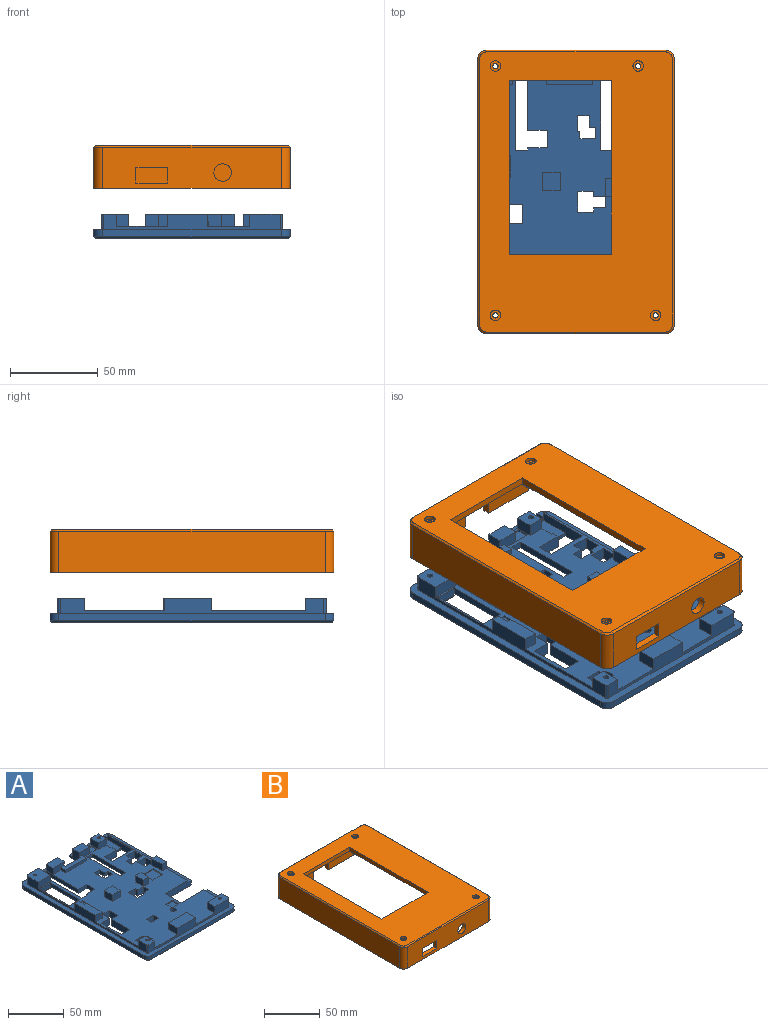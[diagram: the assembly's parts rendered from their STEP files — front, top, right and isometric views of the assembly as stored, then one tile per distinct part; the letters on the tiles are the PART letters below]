
ASSEMBLY  parts=2 mates=1
PART A: 225 faces, bbox 112x162x14 mm
  f0: plane 38.5x4mm, normal (0,1,0), area 103.3mm2, adj f14,f40,f199,f202,f211,f216,f223
  f1: plane 160x110mm, normal (0,0,-1), area 10856.5mm2, adj f25,f51,f87,f88,f89,f90,f91,f92
  f2: plane 42x4mm, normal (-1,0,0), area 168mm2, adj f3,f5,f27,f211
  f3: plane 7x4mm, normal (0,1,0), area 28mm2, adj f2,f4,f27,f211
  f4: plane 42x4mm, normal (1,0,0), area 168mm2, adj f3,f5,f27,f211
  f5: plane 7x4mm, normal (0,-1,0), area 28mm2, adj f2,f4,f27,f211
  f6: plane 6.5x4mm, normal (-1,0,0), area 26mm2, adj f7,f13,f27,f211
  f7: plane 4x3.75mm, normal (0,-1,0), area 15mm2, adj f6,f8,f27,f211
  f8: plane 6.5x4mm, normal (-1,0,0), area 26mm2, adj f7,f9,f27,f211
  f9: plane 9x4mm, normal (0,1,0), area 36mm2, adj f8,f10,f27,f211
  f10: plane 4x4mm, normal (1,0,0), area 16mm2, adj f9,f11,f27,f211
  f11: plane 4x1.25mm, normal (0,1,0), area 5mm2, adj f10,f12,f27,f211
  f12: plane 9x4mm, normal (1,0,0), area 36mm2, adj f11,f13,f27,f211
  f13: plane 6.5x4mm, normal (0,-1,0), area 26mm2, adj f6,f12,f27,f211
  f14: plane 15x11mm, normal (1,0,0), area 119.2mm2, adj f0,f16,f26,f40,f44,f70,f193,f211
  f15: plane 15x11mm, normal (-1,0,0), area 119.2mm2, adj f16,f39,f41,f43,f47,f73,f193,f211
  f16: plane 19x7mm, normal (0,1,0), area 133mm2, adj f14,f15,f193,f211
  f17: plane 40.6x4mm, normal (-1,0,0), area 162.4mm2, adj f18,f24,f27,f211
  f18: plane 11x4mm, normal (0,-1,0), area 44mm2, adj f17,f19,f27,f211
  f19: plane 10x4mm, normal (-1,0,0), area 40mm2, adj f18,f20,f27,f211
  f20: plane 11x4mm, normal (0,1,0), area 44mm2, adj f19,f21,f27,f211
  f21: plane 4x1.5mm, normal (-1,0,0), area 6mm2, adj f20,f22,f27,f211
  f22: plane 7x4mm, normal (0,1,0), area 28mm2, adj f21,f23,f27,f211
  f23: plane 52.1x4mm, normal (1,0,0), area 208.4mm2, adj f22,f24,f27,f211
  f24: plane 7x4mm, normal (0,-1,0), area 28mm2, adj f17,f23,f27,f211
  f25: plane 25.73x1mm, normal (0,0.71,-0.71), area 35.7mm2, adj f1,f47,f210,f224
  f26: plane 14.33x7mm, normal (0,-1,0), area 86.7mm2, adj f14,f27,f70,f71,f190,f193
  f27: plane 153.6x103.6mm, normal (0,0,1), area 10230.7mm2, adj f2,f3,f4,f5,f6,f7,f8,f9
  f28: plane 27.15x7.8mm, normal (0,0,1), area 191.8mm2, adj f29,f30,f50,f62,f170,f173
  f29: plane 7x5.11mm, normal (0,1,0), area 35.8mm2, adj f27,f28,f50,f173
  f30: plane 19.72x7mm, normal (1,0,0), area 138mm2, adj f27,f28,f62,f170
  f31: plane 17.72x12mm, normal (1,0,0), area 160.7mm2, adj f27,f43,f67,f69,f100,f167
  f32: plane 105x6.5mm, normal (0,0,1), area 445.8mm2, adj f33,f38,f47,f56,f123,f166,f194,f200
  f33: plane 3x1mm, normal (0,-1,0), area 3mm2, adj f32,f101,f166,f167
  f34: cylinder r=1.5mm len=11.5mm, axis (0,0,1), area 108.4mm2, adj f67,f165
  f35: cylinder r=1.5mm len=11.5mm, axis (0,0,1), area 108.4mm2, adj f54,f158
  f36: cylinder r=1.5mm len=11.5mm, axis (0,0,1), area 108.4mm2, adj f49,f151
  f37: cylinder r=1.5mm len=11.5mm, axis (0,0,1), area 108.4mm2, adj f74,f144
  f38: plane 100x4mm, normal (1,0,0), area 400mm2, adj f32,f123,f200,f209
  f39: plane 12.67x8.8mm, normal (0,0,1), area 111.5mm2, adj f15,f43,f72,f73
  f40: plane 162x112mm, normal (0,0,1), area 1421.3mm2, adj f0,f14,f42,f44,f45,f46,f48,f50
  f41: plane 32x4.2mm, normal (0,0,1), area 134.4mm2, adj f15,f43,f47,f168
  f42: plane 31.3x9mm, normal (1,0,0), area 120.7mm2, adj f27,f40,f54,f55,f124,f195
  f43: plane 32.5x12mm, normal (0,1,0), area 221.7mm2, adj f15,f27,f31,f39,f41,f67,f68,f72
  f44: plane 37.8x9mm, normal (0,1,0), area 276.1mm2, adj f14,f27,f40,f70,f71,f74,f76,f196
  f45: plane 102x4mm, normal (0,-1,0), area 408mm2, adj f40,f198,f201,f206
  f46: plane 152x4mm, normal (-1,0,0), area 608mm2, adj f40,f198,f199,f204
  f47: plane 44.5x4mm, normal (0,1,0), area 107.9mm2, adj f15,f25,f32,f41,f166,f167,f168,f200
  f48: plane 32x4mm, normal (1,0,0), area 128mm2, adj f40,f124,f201,f208
  f49: plane 11.8x8.8mm, normal (0,0,1), area 96.3mm2, adj f36,f50,f51,f52,f53,f197
  f50: plane 150.6x9mm, normal (-1,0,0), area 659.9mm2, adj f27,f28,f29,f40,f49,f51,f62,f74
  f51: plane 17.3x14mm, normal (0,1,0), area 149.1mm2, adj f1,f27,f49,f50,f52,f118,f122
  f52: plane 11.8x7mm, normal (1,0,0), area 82.6mm2, adj f27,f49,f51,f53
  f53: plane 100.6x9mm, normal (0,-1,0), area 534.4mm2, adj f27,f40,f49,f52,f54,f57,f58,f59
  f54: plane 18.8x9.8mm, normal (0,0,1), area 176.7mm2, adj f35,f42,f53,f55,f57,f195
  f55: plane 18.8x7mm, normal (0,1,0), area 131.6mm2, adj f27,f42,f54,f57
  f56: plane 99.31x9mm, normal (1,0,0), area 291.7mm2, adj f27,f32,f63,f64,f66,f123,f194
  f57: plane 9.8x7mm, normal (-1,0,0), area 68.6mm2, adj f27,f53,f54,f55
  f58: plane 23x11.8mm, normal (0,0,1), area 271.4mm2, adj f53,f59,f60,f61
  f59: plane 11.8x7mm, normal (-1,0,0), area 82.6mm2, adj f27,f53,f58,f60
  f60: plane 23x7mm, normal (0,1,0), area 161mm2, adj f27,f58,f59,f61
  f61: plane 11.8x7mm, normal (1,0,0), area 82.6mm2, adj f27,f53,f58,f60
  f62: plane 7.8x7mm, normal (0,-1,0), area 54.6mm2, adj f27,f28,f30,f50
  f63: plane 13.3x5.8mm, normal (0,0,1), area 77.1mm2, adj f56,f64,f65,f66
  f64: plane 7x5.8mm, normal (0,-1,0), area 40.6mm2, adj f27,f56,f63,f65
  f65: plane 13.3x7mm, normal (-1,0,0), area 93.1mm2, adj f27,f63,f64,f66
  f66: plane 7x5.8mm, normal (0,1,0), area 40.6mm2, adj f27,f56,f63,f65
  f67: plane 10.3x9.5mm, normal (0,0,1), area 90.8mm2, adj f31,f34,f43,f68,f69
  f68: plane 10.3x7mm, normal (-1,0,0), area 72.1mm2, adj f27,f43,f67,f69
  f69: plane 9.5x7mm, normal (0,-1,0), area 66.5mm2, adj f27,f31,f67,f68
  f70: plane 14.33x8.8mm, normal (0,0,1), area 126.1mm2, adj f14,f26,f44,f71
  f71: plane 8.8x7mm, normal (-1,0,0), area 61.6mm2, adj f26,f27,f44,f70
  f72: plane 8.8x7mm, normal (1,0,0), area 61.6mm2, adj f27,f39,f43,f73
  f73: plane 12.67x7mm, normal (0,-1,0), area 79.4mm2, adj f15,f27,f39,f72,f192,f193
  f74: plane 15.81x15.3mm, normal (0,0,1), area 234.3mm2, adj f37,f44,f50,f75,f76,f196
  f75: plane 15.81x7mm, normal (0,-1,0), area 110.6mm2, adj f27,f50,f74,f76
  f76: plane 15.3x7mm, normal (1,0,0), area 107.1mm2, adj f27,f44,f74,f75
  f77: plane 10x10mm, normal (0,0,1), area 100mm2, adj f78,f79,f80,f81
  f78: plane 10x7mm, normal (-1,0,0), area 70mm2, adj f27,f77,f79,f81
  f79: plane 10x7mm, normal (0,-1,0), area 70mm2, adj f27,f77,f78,f80
  f80: plane 10x7mm, normal (1,0,0), area 70mm2, adj f27,f77,f79,f81
  f81: plane 10x7mm, normal (0,1,0), area 70mm2, adj f27,f77,f78,f80
  f82: plane 10x7mm, normal (0,0,1), area 70mm2, adj f83,f84,f85,f86
  f83: plane 10x7mm, normal (1,0,0), area 70mm2, adj f27,f82,f84,f86
  f84: plane 7x7mm, normal (0,1,0), area 49mm2, adj f27,f82,f83,f85
  f85: plane 10x7mm, normal (-1,0,0), area 70mm2, adj f27,f82,f84,f86
  f86: plane 7x7mm, normal (0,-1,0), area 49mm2, adj f27,f82,f83,f85
  f87: plane 25x7mm, normal (1,0,0), area 175mm2, adj f1,f27,f88,f94
  f88: plane 10.78x7mm, normal (0,-1,0), area 75.5mm2, adj f1,f27,f87,f89
  f89: plane 9x7mm, normal (1,0,0), area 63mm2, adj f1,f27,f88,f90
  f90: plane 8x7mm, normal (0,-1,0), area 56mm2, adj f1,f27,f89,f91
  f91: plane 11x7mm, normal (-1,0,0), area 77mm2, adj f1,f27,f90,f92
  f92: plane 8x7mm, normal (0,1,0), area 56mm2, adj f1,f27,f91,f93
  f93: plane 23x7mm, normal (-1,0,0), area 161mm2, adj f1,f27,f92,f94
  f94: plane 10.78x7mm, normal (0,1,0), area 75.5mm2, adj f1,f27,f87,f93
  f95: cylinder r=2.75mm len=7mm, axis (0,0,-1), area 121mm2, adj f1,f27
  f96: plane 25.5x7mm, normal (0,1,0), area 177.6mm2, adj f1,f27,f97,f101,f213,f217
  f97: plane 9.5x4mm, normal (1,0,0), area 38mm2, adj f27,f96,f98,f211
  f98: plane 15x7mm, normal (0,-1,0), area 104.1mm2, adj f1,f27,f97,f99,f214,f224
  f99: plane 7x4.58mm, normal (1,0,0), area 32.1mm2, adj f1,f27,f98,f100,f169
  f100: plane 5x1mm, normal (0,1,0), area 5mm2, adj f27,f31,f99,f167
  f101: plane 31.8x7mm, normal (-1,0,0), area 187.2mm2, adj f1,f27,f33,f96,f167,f169,f194
  f102: plane 10x7mm, normal (-1,0,0), area 70mm2, adj f1,f27,f103,f107
  f103: plane 7x6.8mm, normal (0,1,0), area 47.6mm2, adj f1,f27,f102,f104
  f104: plane 7x2.5mm, normal (-1,0,0), area 17.5mm2, adj f1,f27,f103,f105
  f105: plane 9.5x7mm, normal (0,1,0), area 66.5mm2, adj f1,f27,f104,f106
  f106: plane 7x6.5mm, normal (1,0,0), area 45.5mm2, adj f1,f27,f105,f108
  f107: plane 10x7mm, normal (0,-1,0), area 70mm2, adj f1,f27,f102,f109
  f108: plane 7x6.3mm, normal (0,-1,0), area 44.1mm2, adj f1,f27,f106,f109
  f109: plane 7x6mm, normal (1,0,0), area 42mm2, adj f1,f27,f107,f108
  f110: plane 10x7mm, normal (-1,0,0), area 70mm2, adj f1,f27,f111,f113
  f111: plane 10x7mm, normal (0,1,0), area 70mm2, adj f1,f27,f110,f112
  f112: plane 10x7mm, normal (1,0,0), area 70mm2, adj f1,f27,f111,f113
  f113: plane 10x7mm, normal (0,-1,0), area 70mm2, adj f1,f27,f110,f112
  f114: plane 37x4mm, normal (-1,0,0), area 148mm2, adj f27,f115,f117,f211
  f115: plane 13.2x5mm, normal (0,1,0), area 66mm2, adj f27,f114,f116,f212,f220
  f116: plane 37x5mm, normal (1,0,0), area 185mm2, adj f27,f115,f117,f221
  f117: plane 13.2x5mm, normal (0,-1,0), area 66mm2, adj f27,f114,f116,f216,f222
  f118: plane 9x7mm, normal (1,0,0), area 63mm2, adj f1,f27,f51,f119
  f119: plane 9x7mm, normal (0,-1,0), area 63mm2, adj f1,f27,f118,f120
  f120: plane 7x3.5mm, normal (-1,0,0), area 24.5mm2, adj f1,f27,f119,f121
  f121: plane 7x3.5mm, normal (0,-1,0), area 24.5mm2, adj f1,f27,f120,f122
  f122: plane 7x5.5mm, normal (-1,0,0), area 38.5mm2, adj f1,f27,f51,f121
  f123: plane 33x7mm, normal (0,-1,0), area 222.1mm2, adj f1,f27,f32,f38,f56,f125,f209
  f124: plane 33x7mm, normal (0,1,0), area 222.1mm2, adj f1,f27,f40,f42,f48,f125,f208
  f125: plane 20x7mm, normal (1,0,0), area 140mm2, adj f1,f27,f123,f124
  f126: plane 9x7mm, normal (0,1,0), area 63mm2, adj f1,f27,f127,f129
  f127: plane 7x6.5mm, normal (1,0,0), area 45.5mm2, adj f1,f27,f126,f128
  f128: plane 9x7mm, normal (0,-1,0), area 63mm2, adj f1,f27,f127,f129
  f129: plane 7x6.5mm, normal (-1,0,0), area 45.5mm2, adj f1,f27,f126,f128
  f130: plane 7x2.94mm, normal (-1,0,0), area 20.6mm2, adj f1,f27,f131,f135
  f131: plane 7x7mm, normal (0,-1,0), area 49mm2, adj f1,f27,f130,f132
  f132: plane 7x6.5mm, normal (-1,0,0), area 45.5mm2, adj f1,f27,f131,f133
  f133: plane 7x7mm, normal (0,1,0), area 49mm2, adj f1,f27,f132,f134
  f134: plane 7x2.5mm, normal (-1,0,0), area 17.5mm2, adj f1,f27,f133,f136
  f135: plane 9x7mm, normal (0,-1,0), area 63mm2, adj f1,f27,f130,f137
  f136: plane 9x7mm, normal (0,1,0), area 63mm2, adj f1,f27,f134,f137
  f137: plane 11.94x7mm, normal (1,0,0), area 83.6mm2, adj f1,f27,f135,f136
  f138: plane 2.94x2.5mm, normal (0.5,-0.87,0), area 8.5mm2, adj f1,f139,f143,f144
  f139: plane 2.94x2.5mm, normal (-0.5,-0.87,0), area 8.5mm2, adj f1,f138,f140,f144
  f140: plane 3.4x2.5mm, normal (-1,0,0), area 8.5mm2, adj f1,f139,f141,f144
  f141: plane 2.94x2.5mm, normal (-0.5,0.87,0), area 8.5mm2, adj f1,f140,f142,f144
  f142: plane 2.94x2.5mm, normal (0.5,0.87,0), area 8.5mm2, adj f1,f141,f143,f144
  f143: plane 3.4x2.5mm, normal (1,0,0), area 8.5mm2, adj f1,f138,f142,f144
  f144: plane 6.8x5.89mm, normal (0,0,-1), area 23mm2, adj f37,f138,f139,f140,f141,f142,f143
  f145: plane 3.4x2.5mm, normal (-1,0,0), area 8.5mm2, adj f1,f146,f150,f151
  f146: plane 2.94x2.5mm, normal (-0.5,0.87,0), area 8.5mm2, adj f1,f145,f147,f151
  f147: plane 2.94x2.5mm, normal (0.5,0.87,0), area 8.5mm2, adj f1,f146,f148,f151
  f148: plane 3.4x2.5mm, normal (1,0,0), area 8.5mm2, adj f1,f147,f149,f151
  f149: plane 2.94x2.5mm, normal (0.5,-0.87,0), area 8.5mm2, adj f1,f148,f150,f151
  f150: plane 2.94x2.5mm, normal (-0.5,-0.87,0), area 8.5mm2, adj f1,f145,f149,f151
  f151: plane 6.8x5.89mm, normal (0,0,-1), area 23mm2, adj f36,f145,f146,f147,f148,f149,f150
  f152: plane 2.94x2.5mm, normal (0.87,-0.5,0), area 8.5mm2, adj f1,f153,f157,f158
  f153: plane 3.4x2.5mm, normal (0,-1,0), area 8.5mm2, adj f1,f152,f154,f158
  f154: plane 2.94x2.5mm, normal (-0.87,-0.5,0), area 8.5mm2, adj f1,f153,f155,f158
  f155: plane 2.94x2.5mm, normal (-0.87,0.5,0), area 8.5mm2, adj f1,f154,f156,f158
  f156: plane 3.4x2.5mm, normal (0,1,0), area 8.5mm2, adj f1,f155,f157,f158
  f157: plane 2.94x2.5mm, normal (0.87,0.5,0), area 8.5mm2, adj f1,f152,f156,f158
  f158: plane 6.8x5.89mm, normal (0,0,-1), area 23mm2, adj f35,f152,f153,f154,f155,f156,f157
  f159: plane 3.4x2.5mm, normal (1,0,0), area 8.5mm2, adj f1,f160,f164,f165
  f160: plane 2.94x2.5mm, normal (0.5,-0.87,0), area 8.5mm2, adj f1,f159,f161,f165
  f161: plane 2.94x2.5mm, normal (-0.5,-0.87,0), area 8.5mm2, adj f1,f160,f162,f165
  f162: plane 3.4x2.5mm, normal (-1,0,0), area 8.5mm2, adj f1,f161,f163,f165
  f163: plane 2.94x2.5mm, normal (-0.5,0.87,0), area 8.5mm2, adj f1,f162,f164,f165
  f164: plane 2.94x2.5mm, normal (0.5,0.87,0), area 8.5mm2, adj f1,f159,f163,f165
  f165: plane 6.8x5.89mm, normal (0,0,-1), area 23mm2, adj f34,f159,f160,f161,f162,f163,f164
  f166: plane 4.2x3mm, normal (-1,0,0), area 12.6mm2, adj f32,f33,f47,f167
  f167: plane 21.92x12mm, normal (0,0,1), area 249.9mm2, adj f31,f33,f43,f47,f100,f101,f166,f168
  f168: plane 4.2x3mm, normal (1,0,0), area 12.6mm2, adj f41,f43,f47,f167
  f169: plane 10.5x2mm, normal (0,-1,0), area 21mm2, adj f1,f99,f101,f167
  f170: plane 9.4x8mm, normal (0,1,0), area 28.2mm2, adj f27,f28,f30,f171,f173,f174
  f171: plane 12.25x1mm, normal (-1,0,0), area 12.2mm2, adj f27,f170,f172,f174
  f172: plane 9.4x1mm, normal (0,-1,0), area 9.4mm2, adj f27,f171,f173,f174
  f173: plane 12.25x8mm, normal (1,0,0), area 64.2mm2, adj f27,f28,f29,f170,f172,f174
  f174: plane 12.25x9.4mm, normal (0,0,1), area 115.1mm2, adj f170,f171,f172,f173
  f175: plane 12.39x1mm, normal (0,1,0), area 12.4mm2, adj f27,f176,f178,f179
  f176: plane 11.97x1mm, normal (-1,0,0), area 12mm2, adj f27,f175,f177,f179
  f177: plane 12.39x1mm, normal (0,-1,0), area 12.4mm2, adj f27,f176,f178,f179
  f178: plane 11.97x1mm, normal (1,0,0), area 12mm2, adj f27,f175,f177,f179
  f179: plane 12.39x11.97mm, normal (0,0,1), area 148.3mm2, adj f175,f176,f177,f178
  f180: plane 6.94x1mm, normal (1,0,0), area 6.9mm2, adj f27,f181,f183,f184
  f181: plane 9.03x1mm, normal (0,1,0), area 9mm2, adj f27,f180,f182,f184
  f182: plane 6.94x1mm, normal (-1,0,0), area 6.9mm2, adj f27,f181,f183,f184
  f183: plane 9.03x1mm, normal (0,-1,0), area 9mm2, adj f27,f180,f182,f184
  f184: plane 9.03x6.94mm, normal (0,0,1), area 62.7mm2, adj f180,f181,f182,f183
  f185: plane 8.26x1mm, normal (0,1,0), area 8.3mm2, adj f27,f186,f188,f189
  f186: plane 7.93x1mm, normal (-1,0,0), area 7.9mm2, adj f27,f185,f187,f189
  f187: plane 8.26x1mm, normal (0,-1,0), area 8.3mm2, adj f27,f186,f188,f189
  f188: plane 7.93x1mm, normal (1,0,0), area 7.9mm2, adj f27,f185,f187,f189
  f189: plane 8.26x7.93mm, normal (0,0,1), area 65.5mm2, adj f185,f186,f187,f188
  f190: plane 6.54x3mm, normal (-1,0,0), area 19.6mm2, adj f26,f27,f191,f193
  f191: plane 26.65x3mm, normal (0,-1,0), area 80mm2, adj f27,f190,f192,f193
  f192: plane 6.54x3mm, normal (1,0,0), area 19.6mm2, adj f27,f73,f191,f193
  f193: plane 26.65x6.54mm, normal (0,0,1), area 136.2mm2, adj f14,f15,f16,f26,f73,f190,f191,f192
  f194: cylinder r=1.5mm len=2mm, axis (0,0,1), area 4.3mm2, adj f27,f32,f56,f101
  f195: cylinder r=1.5mm len=9mm, axis (0,0,1), area 21.2mm2, adj f40,f42,f53,f54
  f196: cylinder r=1.5mm len=9mm, axis (0,0,1), area 21.2mm2, adj f40,f44,f50,f74
  f197: cylinder r=1.5mm len=9mm, axis (0,0,-1), area 21.2mm2, adj f40,f49,f50,f53
  f198: cylinder r=5mm len=5mm, axis (0,0,1), area 31.4mm2, adj f40,f45,f46,f205
  f199: cylinder r=5mm len=5mm, axis (0,0,-1), area 31.4mm2, adj f0,f40,f46,f203
  f200: cylinder r=5mm len=5mm, axis (0,0,1), area 31.4mm2, adj f32,f38,f47,f210
  f201: cylinder r=5mm len=5mm, axis (0,0,-1), area 31.4mm2, adj f40,f45,f48,f207
  f202: plane 12.93x1mm, normal (0,0.71,-0.71), area 17.6mm2, adj f0,f1,f203,f223
  f203: cone r=4mm half-angle=45deg, axis (0,0,1), area 10mm2, adj f1,f199,f202,f204
  f204: plane 152x1mm, normal (-0.71,0,-0.71), area 215mm2, adj f1,f46,f203,f205
  f205: cone r=4mm half-angle=45deg, axis (0,0,1), area 10mm2, adj f1,f198,f204,f206
  f206: plane 102x1mm, normal (0,-0.71,-0.71), area 144.2mm2, adj f1,f45,f205,f207
  f207: cone r=4mm half-angle=45deg, axis (0,0,1), area 10mm2, adj f1,f201,f206,f208
  f208: plane 32x1mm, normal (0.71,0,-0.71), area 45.3mm2, adj f1,f48,f124,f207
  f209: plane 100x1mm, normal (0.71,0,-0.71), area 141.4mm2, adj f1,f38,f123,f210
  f210: cone r=4mm half-angle=45deg, axis (0,0,1), area 10mm2, adj f1,f25,f200,f209
  f211: plane 62.8x62.1mm, normal (0,0,-1), area 2742.3mm2, adj f0,f2,f3,f4,f5,f6,f7,f8
  f212: plane 4.6x1mm, normal (1,0,0), area 4.6mm2, adj f115,f211,f215,f219
  f213: plane 26.1x1mm, normal (-1,0,0), area 26.1mm2, adj f96,f211,f215,f217
  f214: plane 26.5x1mm, normal (-1,0,0), area 26.5mm2, adj f47,f98,f211,f224
  f215: plane 62.8x1mm, normal (0,1,0), area 62.8mm2, adj f211,f212,f213,f218
  f216: plane 20.5x1mm, normal (1,0,0), area 20.5mm2, adj f0,f117,f211,f223
  f217: cylinder r=2mm len=28.1mm, axis (0,1,0), area 84.3mm2, adj f1,f96,f213,f218
  f218: cylinder r=2mm len=66.8mm, axis (1,0,0), area 201.9mm2, adj f1,f215,f217,f219
  f219: cylinder r=2mm len=6.6mm, axis (0,-1,0), area 14.5mm2, adj f1,f212,f218,f220
  f220: cylinder r=2mm len=15.2mm, axis (1,0,0), area 41.5mm2, adj f1,f115,f219,f221
  f221: cylinder r=2mm len=41mm, axis (0,-1,0), area 120.8mm2, adj f1,f116,f220,f222
  f222: cylinder r=2mm len=15.2mm, axis (-1,0,0), area 41.5mm2, adj f1,f117,f221,f223
  f223: cylinder r=2mm len=20.5mm, axis (0,-1,0), area 60.7mm2, adj f0,f1,f202,f216,f222
  f224: cylinder r=2mm len=26.5mm, axis (0,1,0), area 81.9mm2, adj f1,f25,f47,f98,f214
PART B: 84 faces, bbox 112x162x24.6 mm
  f0: plane 104x20.6mm, normal (0,1,0), area 1561.9mm2, adj f3,f6,f14,f15,f17,f27,f28,f32
  f1: plane 102x23.6mm, normal (0,-1,0), area 2166.7mm2, adj f6,f67,f68,f69,f70,f71,f73,f74
  f2: plane 77.8x6.5mm, normal (0,0,-1), area 315.8mm2, adj f3,f4,f7,f8,f59,f66,f75
  f3: plane 154x20.6mm, normal (-1,0,0), area 2453.7mm2, adj f0,f2,f6,f7,f15,f17,f25,f26
  f4: plane 152x23.6mm, normal (1,0,0), area 3045.6mm2, adj f2,f6,f62,f63,f64,f65,f66,f74
  f5: plane 32x4mm, normal (0,0,-1), area 128mm2, adj f7,f8,f56,f61
  f6: plane 162x112mm, normal (0,0,-1), area 1353.9mm2, adj f0,f1,f3,f4,f7,f8,f18,f32
  f7: plane 104x18.6mm, normal (0,-1,0), area 1349.6mm2, adj f2,f3,f5,f6,f13,f22,f23,f30
  f8: plane 102x23.6mm, normal (0,1,0), area 2137.2mm2, adj f2,f5,f6,f56,f57,f58,f59,f60
  f9: cylinder r=1.5mm len=12mm, axis (0,0,-1), area 113.1mm2, adj f15,f55
  f10: cylinder r=1.5mm len=12mm, axis (0,0,-1), area 113.1mm2, adj f14,f49
  f11: cylinder r=1.5mm len=12mm, axis (0,0,-1), area 113.1mm2, adj f30,f51
  f12: cylinder r=1.5mm len=12mm, axis (0,0,-1), area 113.1mm2, adj f13,f53
  f13: plane 17x17mm, normal (0,0,-1), area 218.9mm2, adj f7,f12,f19,f20,f21,f22,f32
  f14: plane 17x17mm, normal (0,0,-1), area 226.9mm2, adj f0,f10,f28,f29,f31,f32,f33
  f15: plane 17x12mm, normal (0,0,-1), area 196.9mm2, adj f0,f3,f9,f26,f27
  f16: plane 13.35x10mm, normal (0,-1,0), area 130.8mm2, adj f17,f23,f24,f30,f40,f47
  f17: plane 148.29x104mm, normal (0,0,-1), area 6195.1mm2, adj f0,f3,f16,f19,f24,f25,f26,f27
  f18: plane 152x23.6mm, normal (-1,0,0), area 3587.2mm2, adj f6,f72,f73,f79
  f19: plane 10x10mm, normal (0,-1,0), area 95mm2, adj f13,f17,f20,f32,f42,f47
  f20: plane 9x8mm, normal (1,0,0), area 72mm2, adj f13,f19,f21,f47
  f21: plane 8x7mm, normal (0,-1,0), area 56mm2, adj f13,f20,f22,f47
  f22: plane 8x8mm, normal (1,0,0), area 64mm2, adj f7,f13,f21,f47
  f23: plane 12x8mm, normal (-1,0,0), area 96mm2, adj f7,f16,f30,f47
  f24: plane 10x6.29mm, normal (1,0,0), area 62.9mm2, adj f16,f17,f25,f30
  f25: plane 10x9mm, normal (0,-1,0), area 90mm2, adj f3,f17,f24,f30
  f26: plane 17x10mm, normal (0,1,0), area 170mm2, adj f3,f15,f17,f27
  f27: plane 12x10mm, normal (-1,0,0), area 120mm2, adj f0,f15,f17,f26
  f28: plane 12x10mm, normal (1,0,0), area 120mm2, adj f0,f14,f17,f29
  f29: plane 11x10mm, normal (0,1,0), area 110mm2, adj f14,f17,f28,f31
  f30: plane 22.35x12mm, normal (0,0,-1), area 204.5mm2, adj f3,f7,f11,f16,f23,f24,f25
  f31: plane 10x5mm, normal (1,0,0), area 50mm2, adj f14,f17,f29,f33
  f32: plane 154x20.6mm, normal (1,0,0), area 2832.4mm2, adj f0,f6,f7,f13,f14,f17,f19,f33
  f33: plane 10x6mm, normal (0,1,0), area 60mm2, adj f14,f17,f31,f32
  f34: plane 99x4mm, normal (1,0,0), area 396mm2, adj f35,f37,f38,f39
  f35: plane 58.5x4mm, normal (0,-1,0), area 234mm2, adj f34,f36,f38,f39
  f36: plane 99x4mm, normal (-1,0,0), area 396mm2, adj f35,f37,f38,f39
  f37: plane 58.5x4mm, normal (0,1,0), area 234mm2, adj f34,f36,f38,f39
  f38: plane 160x110mm, normal (0,0,1), area 11681.7mm2, adj f34,f35,f36,f37,f48,f50,f52,f54
  f39: plane 108x69.5mm, normal (0,0,-1), area 1714.5mm2, adj f34,f35,f36,f37,f43,f44,f45,f46
  f40: plane 108x2mm, normal (1,0,0), area 216mm2, adj f16,f17,f41,f47
  f41: plane 75.5x2mm, normal (0,-1,0), area 151mm2, adj f17,f40,f42,f47
  f42: plane 103x2mm, normal (-1,0,0), area 206mm2, adj f17,f19,f41,f47
  f43: plane 108x2mm, normal (1,0,0), area 216mm2, adj f39,f44,f46,f47
  f44: plane 69.5x2mm, normal (0,1,0), area 139mm2, adj f39,f43,f45,f47
  f45: plane 108x2mm, normal (-1,0,0), area 216mm2, adj f39,f44,f46,f47
  f46: plane 69.5x2mm, normal (0,-1,0), area 139mm2, adj f39,f43,f45,f47
  f47: plane 120x75.5mm, normal (0,0,-1), area 1439.3mm2, adj f7,f16,f19,f20,f21,f22,f23,f40
  f48: cylinder r=3mm len=6mm, axis (0,0,1), area 37.7mm2, adj f38,f49
  f49: plane 6x6mm, normal (0,0,1), area 21.2mm2, adj f10,f48
  f50: cylinder r=3mm len=6mm, axis (0,0,1), area 37.7mm2, adj f38,f51
  f51: plane 6x6mm, normal (0,0,1), area 21.2mm2, adj f11,f50
  f52: cylinder r=3mm len=6mm, axis (0,0,1), area 37.7mm2, adj f38,f53
  f53: plane 6x6mm, normal (0,0,1), area 21.2mm2, adj f12,f52
  f54: cylinder r=3mm len=6mm, axis (0,0,1), area 37.7mm2, adj f38,f55
  f55: plane 6x6mm, normal (0,0,1), area 21.2mm2, adj f9,f54
  f56: plane 9x4mm, normal (-1,0,0), area 36mm2, adj f5,f7,f8,f58
  f57: plane 9x4mm, normal (1,0,0), area 36mm2, adj f6,f7,f8,f58
  f58: plane 19x4mm, normal (0,0,-1), area 76mm2, adj f7,f8,f56,f57
  f59: plane 9x4mm, normal (-1,0,0), area 36mm2, adj f2,f7,f8,f60
  f60: plane 11x4mm, normal (0,0,-1), area 44mm2, adj f7,f8,f59,f61
  f61: plane 9x4mm, normal (1,0,0), area 36mm2, adj f5,f7,f8,f60
  f62: plane 29.2x4mm, normal (0,0,-1), area 116.8mm2, adj f3,f4,f63,f66
  f63: plane 4x4mm, normal (0,1,0), area 16mm2, adj f3,f4,f62,f64
  f64: plane 18x4mm, normal (0,0,-1), area 72mm2, adj f3,f4,f63,f65
  f65: plane 9x4mm, normal (0,1,0), area 36mm2, adj f3,f4,f6,f64
  f66: plane 13x4mm, normal (0,-1,0), area 52mm2, adj f2,f3,f4,f62
  f67: cylinder r=5mm len=10mm, axis (0,-1,0), area 125.7mm2, adj f0,f1
  f68: plane 18x4mm, normal (0,0,1), area 72mm2, adj f0,f1,f69,f71
  f69: plane 9x4mm, normal (-1,0,0), area 36mm2, adj f0,f1,f68,f70
  f70: plane 18x4mm, normal (0,0,-1), area 72mm2, adj f0,f1,f69,f71
  f71: plane 9x4mm, normal (1,0,0), area 36mm2, adj f0,f1,f68,f70
  f72: cylinder r=5mm len=23.6mm, axis (0,0,1), area 185.4mm2, adj f6,f8,f18,f81
  f73: cylinder r=5mm len=23.6mm, axis (0,0,-1), area 185.4mm2, adj f1,f6,f18,f77
  f74: cylinder r=5mm len=23.6mm, axis (0,0,1), area 185.4mm2, adj f1,f4,f6,f78
  f75: cylinder r=5mm len=23.6mm, axis (0,0,-1), area 185.4mm2, adj f2,f4,f8,f82
  f76: plane 102x1mm, normal (0,-0.71,0.71), area 144.2mm2, adj f1,f38,f77,f78
  f77: cone r=4mm half-angle=45deg, axis (0,0,-1), area 10mm2, adj f38,f73,f76,f79
  f78: cone r=4mm half-angle=45deg, axis (0,0,-1), area 10mm2, adj f38,f74,f76,f80
  f79: plane 152x1mm, normal (-0.71,0,0.71), area 215mm2, adj f18,f38,f77,f81
  f80: plane 152x1mm, normal (0.71,0,0.71), area 215mm2, adj f4,f38,f78,f82
  f81: cone r=4mm half-angle=45deg, axis (0,0,-1), area 10mm2, adj f38,f72,f79,f83
  f82: cone r=4mm half-angle=45deg, axis (0,0,-1), area 10mm2, adj f38,f75,f80,f83
  f83: plane 102x1mm, normal (0,0.71,0.71), area 144.2mm2, adj f8,f38,f81,f82
PLACE A t=(-2.22,19.1,14)mm
PLACE B t=(-2.22,19.1,37.78)mm
MATE slider B.f9 <-> A.f35  axis (0,0,-1) through (43.28,-51.4,39.38)mm
